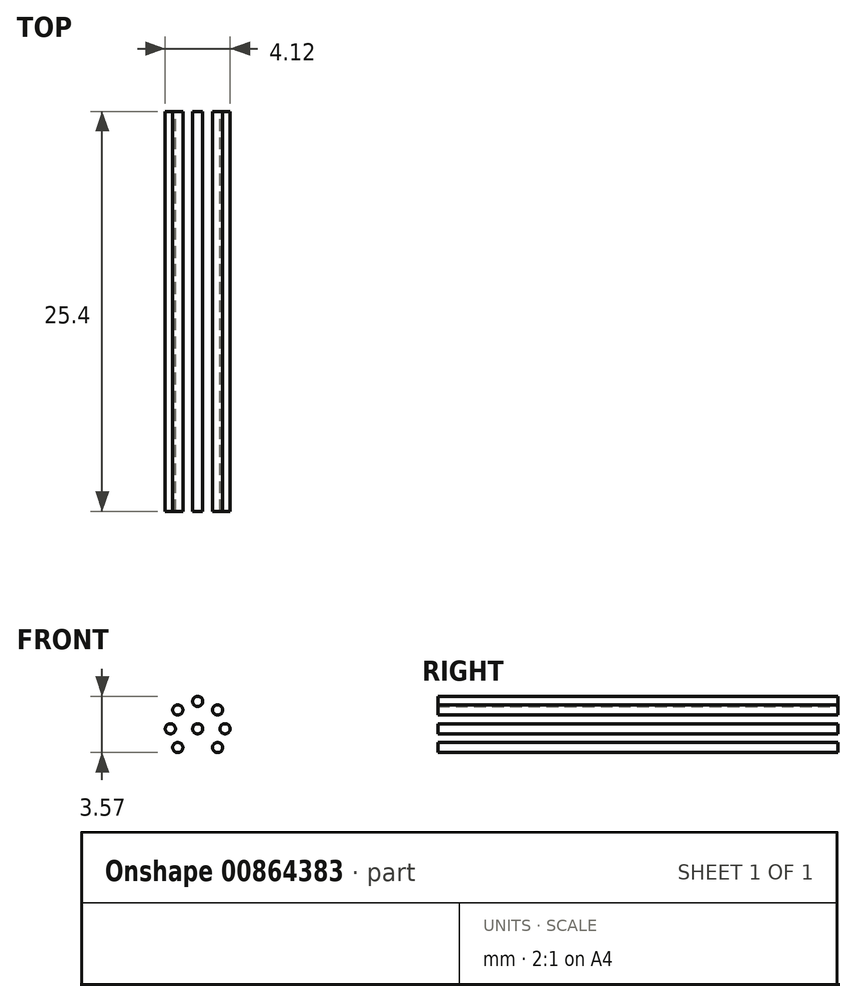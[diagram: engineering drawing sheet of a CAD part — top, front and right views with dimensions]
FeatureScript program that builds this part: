
annotation { "Feature Type Name" : "Feature", "Feature Type Description" : "" }
export const myFeature = defineFeature(function(context is Context, id is Id, definition is map)
    precondition{}
    {
        {
            var Q0;
            Q0=qCreatedBy(makeId("Front.planeOp"),FACE);
            var sketch = newSketch(context, id + "F0", { "sketchPlane" : qUnion([Q0])});
            skCircle(sketch, "E0", {"center": v(0, 0) * mm, "radius": 2.5 * mm});
            skCircle(sketch, "E1", {"center": v(0, 0) * mm, "radius": 0.32 * mm});
            skCircle(sketch, "E2", {"center": v(0, 1.74) * mm, "radius": 0.32 * mm});
            skCircle(sketch, "E3", {"center": v(-1.74, 0) * mm, "radius": 0.32 * mm});
            skCircle(sketch, "E4", {"center": v(1.74, 0) * mm, "radius": 0.32 * mm});
            skCircle(sketch, "E5", {"center": v(-1.26, 1.2) * mm, "radius": 0.32 * mm});
            skCircle(sketch, "E6", {"center": v(1.26, 1.2) * mm, "radius": 0.32 * mm});
            skCircle(sketch, "E7", {"center": v(-1.26, -1.2) * mm, "radius": 0.32 * mm});
            skCircle(sketch, "E8", {"center": v(1.26, -1.2) * mm, "radius": 0.32 * mm});
            skSolve(sketch);
        }
        {
            var Q0;
            Q0=makeQuery(id+"F0.imprint","IMPRINT",FACE,{"disambiguationData":[TD([[makeQuery(id+"F0.imprint","IMPRINT",EDGE,{"derivedFrom":sQuery(id+"F0.wireOp",EDGE,"E4")}),1.0]])]});
            var Q1;
            Q1=makeQuery(id+"F0.imprint","IMPRINT",FACE,{"disambiguationData":[TD([[makeQuery(id+"F0.imprint","IMPRINT",EDGE,{"derivedFrom":sQuery(id+"F0.wireOp",EDGE,"E8")}),1.0]])]});
            var Q2;
            Q2=makeQuery(id+"F0.imprint","IMPRINT",FACE,{"disambiguationData":[TD([[makeQuery(id+"F0.imprint","IMPRINT",EDGE,{"derivedFrom":sQuery(id+"F0.wireOp",EDGE,"E6")}),1.0]])]});
            var Q3;
            Q3=makeQuery(id+"F0.imprint","IMPRINT",FACE,{"disambiguationData":[TD([[makeQuery(id+"F0.imprint","IMPRINT",EDGE,{"derivedFrom":sQuery(id+"F0.wireOp",EDGE,"E1")}),1.0]])]});
            var Q4;
            Q4=makeQuery(id+"F0.imprint","IMPRINT",FACE,{"disambiguationData":[TD([[makeQuery(id+"F0.imprint","IMPRINT",EDGE,{"derivedFrom":sQuery(id+"F0.wireOp",EDGE,"E7")}),1.0]])]});
            var Q5;
            Q5=makeQuery(id+"F0.imprint","IMPRINT",FACE,{"disambiguationData":[TD([[makeQuery(id+"F0.imprint","IMPRINT",EDGE,{"derivedFrom":sQuery(id+"F0.wireOp",EDGE,"E3")}),1.0]])]});
            var Q6;
            Q6=makeQuery(id+"F0.imprint","IMPRINT",FACE,{"disambiguationData":[TD([[makeQuery(id+"F0.imprint","IMPRINT",EDGE,{"derivedFrom":sQuery(id+"F0.wireOp",EDGE,"E5")}),1.0]])]});
            var Q7;
            Q7=makeQuery(id+"F0.imprint","IMPRINT",FACE,{"disambiguationData":[TD([[makeQuery(id+"F0.imprint","IMPRINT",EDGE,{"derivedFrom":sQuery(id+"F0.wireOp",EDGE,"E2")}),1.0]])]});
            extrude(context, id + "F1", {"entities" : qUnion([Q0, Q1, Q2, Q3, Q4, Q5, Q6, Q7]), "depth" : 25.4 * mm, "offsetDistance" : 25.4 * mm});
        }
    });
